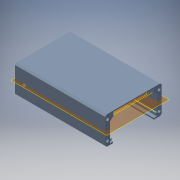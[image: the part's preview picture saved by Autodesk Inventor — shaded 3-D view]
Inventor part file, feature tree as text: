
AUTODESK INVENTOR PART (.ipt)
format: ipt  version: 2019.4 (Build 234330000, 330)  size: 493,568 bytes
history: native  units: mm
features: reference x12, sketch x11, extrude x11, other x11, plane x10, projected_geometry x9, chamfer x4, mirror x1
ambient origin geometry x8: Origin, YZ Plane, XZ Plane, XY Plane, X Axis, Y Axis, Z Axis, Center Point
bodies: Volumenkörper2 (feature_tree)
feature tree (69):
  plane  "Arbeitsebene6"
  sketch  "Skizze6"  dims[d39=1.0mm d42=0.1mm]
  plane  "Arbeitsebene7"
  extrude  "Extrusion6"  Depth=0.1mm
  extrude  "Extrusion7"  Depth=2.0mm
  plane  "Arbeitsebene8"
  extrude  "Extrusion8"  Depth=3.9mm
  chamfer  "Fase1"  Distance=2.0mm
  chamfer  "Fase2"  Distance=50.0mm
  extrude  "Extrusion10"  Depth=2.0mm TaperAngle=45.0deg
  sketch  "Skizze12"  dims[d58=8.9mm d72=50.0mm d73=0.0mm]
  plane  "Arbeitsebene9"
  extrude  "Extrusion11"  Depth=10.0mm TaperAngle=0.0deg
  extrude  "Extrusion12"  Depth=8.0mm TaperAngle=0.0deg
  chamfer  "Fase4"  Distance=2.0mm Angle=45.0deg
  plane  "Arbeitsebene10"
  chamfer  "Fase5"  Distance=0.65mm
  other  "Arbeitspunkt3"
  plane  "Arbeitsebene11"
  extrude  "Extrusion17"  Depth=2.0mm TaperAngle=45.0deg
  mirror  "Spiegeln2"
  extrude  "Extrusion21"  Depth=2.0mm
  extrude  "Extrusion22"  Depth=2.0mm
  extrude  "Extrusion23"  Depth=10.0mm TaperAngle=0.0deg
  extrude  "Extrusion24"  Depth=2.0mm
  reference  "Referenz13"
  reference  "Referenz14"
  reference  "Referenz15"
  reference  "Referenz16"
  reference  "Referenz17"
  reference  "Referenz18"
  reference  "Referenz19"
  reference  "Referenz20"
  reference  "Referenz21"
  reference  "Referenz22"
  reference  "Referenz23"
  sketch  "Skizze7"  dims[d43=2.0mm d44=0.0mm d48=4.3mm]
  projected_geometry  "Projizierte Kontur5"
  sketch  "Skizze8"  dims[d51=17.4mm d52=17.9mm d53=3.9mm]
  sketch  "Skizze11"  dims[d54=8.9mm d56=2.0mm d57=0.0mm]
  projected_geometry  "Projizierte Kontur8"
  sketch  "Skizze13"  dims[d87=1.0mm d88=2.0mm d89=45.0deg d90=1.0mm d91=2.0mm d92=45.0deg]
  other  "Arbeitsachse1"
  sketch  "Skizze18"  dims[d93=2.8mm d94=10.0mm d95=0.0mm]
  projected_geometry  "Projizierte Kontur14"
  projected_geometry  "Projizierte Kontur18"
  plane  "Arbeitsebene16"
  plane  "Arbeitsebene17"
  plane  "Arbeitsebene18"
  plane  "Arbeitsebene19"
  other  "Arbeitspunkt4"
  sketch  "Skizze22"  dims[d96=13.0mm d97=0.0mm d103=8.0mm d104=0.0mm]
  projected_geometry  "Projizierte Kontur19"
  sketch  "Skizze23"  dims[d113=36.0mm d126=3.0mm d127=2.0mm d128=45.0deg]
  projected_geometry  "Projizierte Kontur20"
  reference  "Referenz48"
  sketch  "Skizze24"  dims[d132=0.0mm]
  projected_geometry  "Projizierte Kontur21"
  projected_geometry  "Projizierte Kontur22"
  sketch  "Sketch25"  dims[d135=0.75mm d136=0.65mm d137=1.0mm d138=2.0mm d139=45.0deg d141=8.4mm d142=0.2mm d143=10.0mm d144=0.0mm d157=2.5mm d160=17.9mm d161=8.9mm d162=1.7mm d163=3.5mm d164=3.5mm d166=3.5mm d167=0.75mm d168=2.5mm d169=2.8mm d170=1.0mm d171=0.0mm d172=2.0mm d175=2.0mm d178=1.0mm d179=0.0mm d180=1.0mm d181=0.0mm d182=3.0mm d183=3.0mm d184=0.0mm d185=0.0mm d186=1.0mm d187=1.0mm d188=1.0mm d189=1.0mm d190=1.9mm d191=1.9mm d192=2.0mm d193=0.0mm]
  projected_geometry  "Projected Loop23"
  other  "<userpath>\Documents\Inventor\HITscope\HITscope_v0.iam"
  other  "HITscope_v0.iam"
  other  "00_ESP32_Board:1"
  other  "Assembly_Omniscope_v1.iam"
  other  "01_Camera_Module_Lit:1"
  other  "<userpath>\Documents\Inventor\HITscope\Assembly_HITscope.iam"
  other  "Assembly_HITscope.iam"
  other  "HITscope_v0:1"
